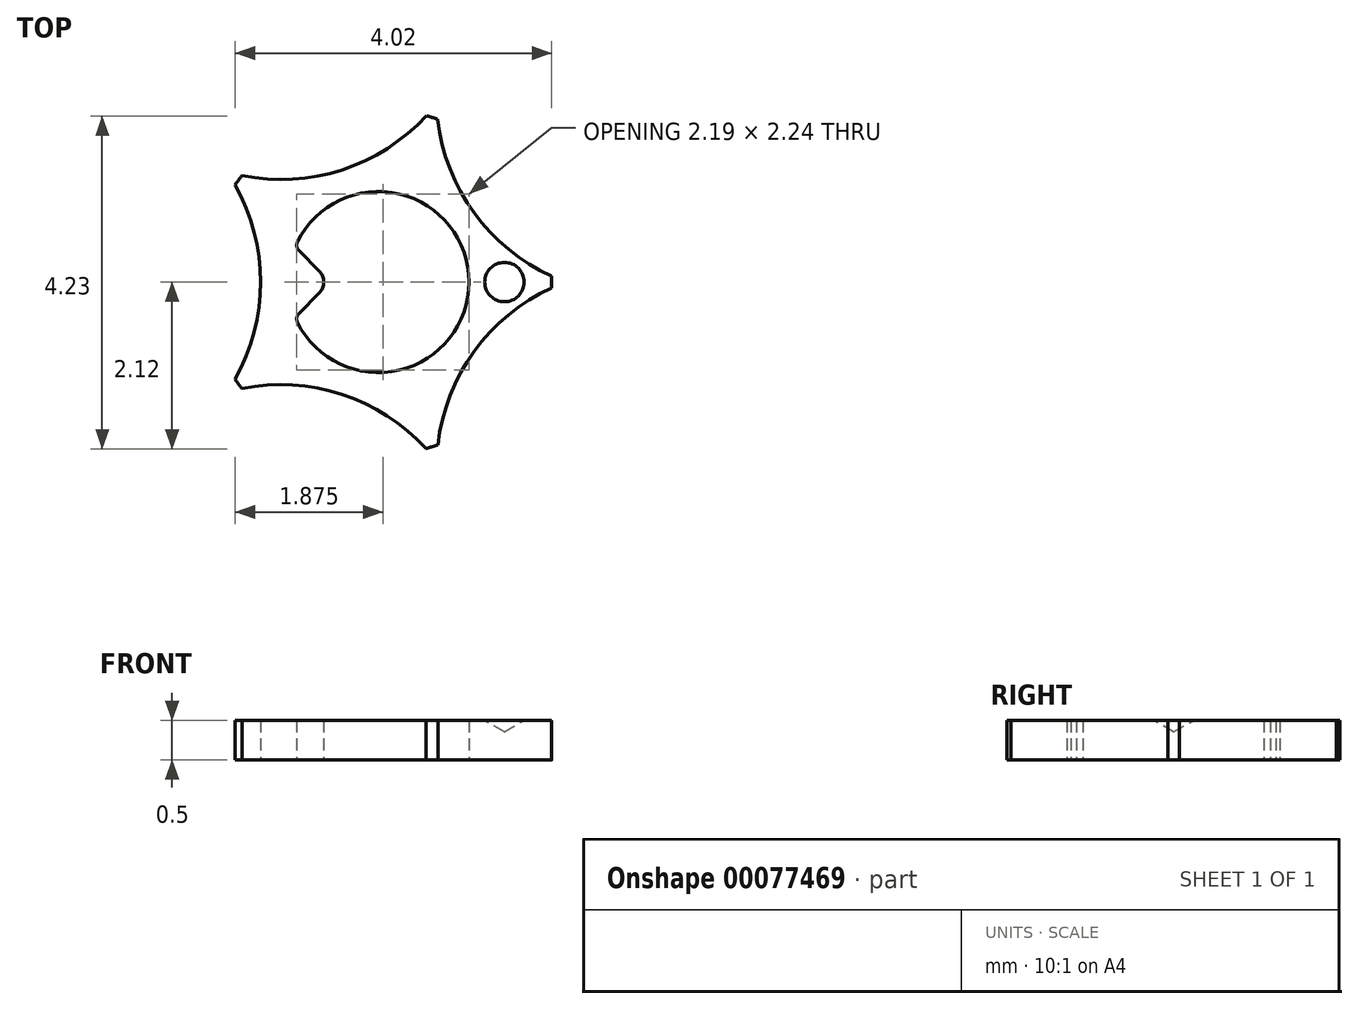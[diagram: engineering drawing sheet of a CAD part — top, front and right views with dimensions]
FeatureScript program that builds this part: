
annotation { "Feature Type Name" : "Feature", "Feature Type Description" : "" }
export const myFeature = defineFeature(function(context is Context, id is Id, definition is map)
    precondition{}
    {
        {
            var Q0;
            Q0=qCreatedBy(makeId("Top.planeOp"),FACE);
            var sketch = newSketch(context, id + "F0", { "sketchPlane" : qUnion([Q0])});
            skArc(sketch, "E0", {"start": v(-1.03, -0.51) * mm, "mid": v(1.15, 0) * mm, "end": v(-1.03, 0.51) * mm});
            skArc(sketch, "E1", {"start": v(-1.73, 1.35) * mm, "mid": v(-1.78, 1.3) * mm, "end": v(-1.82, 1.23) * mm});
            skLineSegment(sketch, "E2", {"start": v(0, 0) * mm, "end": v(2.2, 0) * mm, "construction": true});
            skLineSegment(sketch, "E3", {"start": v(0, 0) * mm, "end": v(0.68, -2.1) * mm, "construction": true});
            skLineSegment(sketch, "E4", {"start": v(0, 0) * mm, "end": v(-1.78, -1.3) * mm, "construction": true});
            skLineSegment(sketch, "E5", {"start": v(0, 0) * mm, "end": v(-1.78, 1.3) * mm, "construction": true});
            skLineSegment(sketch, "E6", {"start": v(0, 0) * mm, "end": v(0.68, 2.1) * mm, "construction": true});
            skPoint(sketch, "E7.third.point", {"position": v(1.22, -0.88) * mm});
            skPoint(sketch, "E8.third.point", {"position": v(-0.74, -1.3) * mm});
            skPoint(sketch, "E9.third.point", {"position": v(-1.5, 0) * mm});
            skPoint(sketch, "E10.third.point", {"position": v(-0.64, 1.3) * mm});
            skPoint(sketch, "E11.third.point", {"position": v(0.97, 1.29) * mm});
            skPoint(sketch, "E12", {"position": v(2.2, 0.08) * mm});
            skPoint(sketch, "E13", {"position": v(2.2, -0.08) * mm});
            skPoint(sketch, "E14", {"position": v(0.75, -2.07) * mm});
            skPoint(sketch, "E15", {"position": v(0.6, -2.12) * mm});
            skPoint(sketch, "E16", {"position": v(-1.73, -1.35) * mm});
            skPoint(sketch, "E17", {"position": v(-1.82, -1.23) * mm});
            skPoint(sketch, "E18", {"position": v(-1.82, 1.23) * mm});
            skPoint(sketch, "E19", {"position": v(-1.73, 1.35) * mm});
            skPoint(sketch, "E20", {"position": v(0.6, 2.11) * mm});
            skPoint(sketch, "E21", {"position": v(0.75, 2.07) * mm});
            skArc(sketch, "E22", {"start": v(2.2, -0.08) * mm, "mid": v(1.21, -0.88) * mm, "end": v(0.75, -2.07) * mm});
            skArc(sketch, "E23", {"start": v(0.6, -2.12) * mm, "mid": v(-0.46, -1.43) * mm, "end": v(-1.73, -1.35) * mm});
            skPoint(sketch, "E23.third.point", {"position": v(-0.74, -1.35) * mm});
            skArc(sketch, "E24", {"start": v(-1.82, -1.23) * mm, "mid": v(-1.5, 0) * mm, "end": v(-1.82, 1.23) * mm});
            skPoint(sketch, "E25.third.point", {"position": v(-0.74, 1.35) * mm});
            skArc(sketch, "E26", {"start": v(0.75, 2.07) * mm, "mid": v(1.21, 0.88) * mm, "end": v(2.2, 0.08) * mm});
            skPoint(sketch, "E27.third.point", {"position": v(-0.39, 1.4) * mm});
            skArc(sketch, "E28", {"start": v(-1.73, 1.35) * mm, "mid": v(-0.46, 1.43) * mm, "end": v(0.6, 2.11) * mm});
            skPoint(sketch, "E29.orphan", {"position": v(-1.93, 1.4) * mm});
            skLineSegment(sketch, "E30", {"start": v(0, 0) * mm, "end": v(-0.61, 0) * mm, "construction": true});
            skLineSegment(sketch, "E31", {"start": v(-0.75, 0.14) * mm, "end": v(-1.01, 0.4) * mm});
            skLineSegment(sketch, "E32", {"start": v(-0.75, -0.14) * mm, "end": v(-1.01, -0.4) * mm});
            skPoint(sketch, "E33.visualSharp", {"position": v(-0.61, 0) * mm});
            skArc(sketch, "E33.filletArc", {"start": v(-0.75, -0.14) * mm, "mid": v(-0.7, 0) * mm, "end": v(-0.75, 0.14) * mm});
            skPoint(sketch, "E34.visualSharp", {"position": v(-1.06, -0.45) * mm});
            skArc(sketch, "E34.filletArc", {"start": v(-1.01, -0.4) * mm, "mid": v(-1.04, -0.45) * mm, "end": v(-1.03, -0.51) * mm});
            skPoint(sketch, "E35.visualSharp", {"position": v(-1.06, 0.45) * mm});
            skArc(sketch, "E35.filletArc", {"start": v(-1.03, 0.51) * mm, "mid": v(-1.04, 0.45) * mm, "end": v(-1.01, 0.4) * mm});
            skArc(sketch, "E36.trimOffspring", {"start": v(0.75, 2.07) * mm, "mid": v(0.68, 2.1) * mm, "end": v(0.6, 2.11) * mm});
            skArc(sketch, "E37.trimOffspring", {"start": v(2.2, -0.08) * mm, "mid": v(2.2, 0) * mm, "end": v(2.2, 0.08) * mm});
            skArc(sketch, "E38.trimOffspring", {"start": v(0.6, -2.12) * mm, "mid": v(0.68, -2.1) * mm, "end": v(0.75, -2.07) * mm});
            skArc(sketch, "E39.trimOffspring", {"start": v(-1.82, -1.23) * mm, "mid": v(-1.78, -1.3) * mm, "end": v(-1.73, -1.35) * mm});
            skSolve(sketch);
        }
        {
            var Q0;
            Q0=makeQuery(id+"F0.imprint","IMPRINT",FACE,{"disambiguationData":[TD([[makeQuery(id+"F0.imprint","IMPRINT",EDGE,{"derivedFrom":sQuery(id+"F0.wireOp",EDGE,"E0")}),-1.0]])]});
            extrude(context, id + "F1", {"entities" : qUnion([Q0]), "depth" : 0.5 * mm});
        }
        {
            var Q0;
            Q0=qCreatedBy(makeId("Front.planeOp"),FACE);
            var sketch = newSketch(context, id + "F2", { "sketchPlane" : qUnion([Q0])});
            skLineSegment(sketch, "E40", {"start": v(0, 0) * mm, "end": v(0, 0.5) * mm, "construction": true});
            skLineSegment(sketch, "E41", {"start": v(0, 0.5) * mm, "end": v(1.6, 0.5) * mm, "construction": true});
            skLineSegment(sketch, "E42", {"start": v(1.6, 0.5) * mm, "end": v(1.85, 0.5) * mm});
            skLineSegment(sketch, "E43", {"start": v(1.6, 0.5) * mm, "end": v(1.35, 0.5) * mm, "construction": true});
            skLineSegment(sketch, "E44", {"start": v(1.85, 0.5) * mm, "end": v(1.6, 0.36) * mm});
            skLineSegment(sketch, "E45", {"start": v(1.6, 0.36) * mm, "end": v(1.35, 0.5) * mm, "construction": true});
            skLineSegment(sketch, "E46", {"start": v(1.6, 0.5) * mm, "end": v(1.6, 0.36) * mm});
            skSolve(sketch);
        }
        {
            var Q0;
            Q0=makeQuery(id+"F2.imprint","IMPRINT",FACE,{"disambiguationData":[TD([[makeQuery(id+"F2.imprint","IMPRINT",EDGE,{"derivedFrom":sQuery(id+"F2.wireOp",EDGE,"E42")}),-1.0]])]});
            var Q1;
            Q1=sQuery(id+"F2.wireOp",EDGE,"E46");
            revolve(context, id + "F3", {"operationType" : NewBodyOperationType.REMOVE, "entities" : qUnion([Q0]), "axis" : qUnion([Q1]), "revolveType" : RevolveType.FULL, "oppositeDirection" : true});
        }
    });
